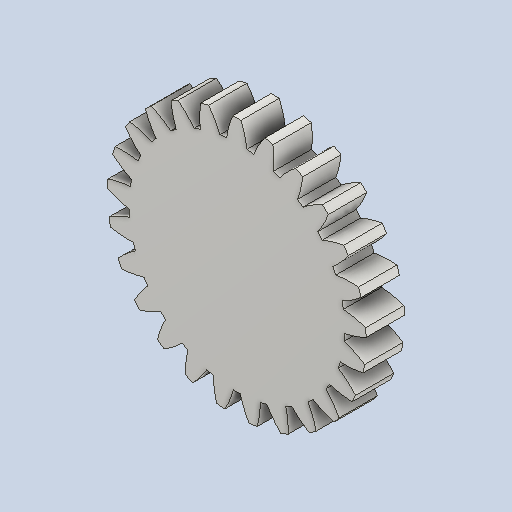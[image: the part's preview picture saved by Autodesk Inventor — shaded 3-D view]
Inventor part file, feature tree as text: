
AUTODESK INVENTOR PART (.ipt)
format: ipt  version: 2024 (Build 280153000, 153)  size: 251,904 bytes
history: native  units: mm (DEFAULTED — no unit token found)
features: plane x3, other x3, extrude x1, sketch x1
ambient origin geometry x8: Origin, YZ Plane, XZ Plane, XY Plane, X Axis, Y Axis, Z Axis, Center Point
bodies: Solid1 (feature_tree)
feature tree (8):
  extrude  "Extrusion1"  Depth=20.0mm TaperAngle=0.0deg
  plane  "Work Plane2"
  plane  "Work Plane8"
  plane  "Work Plane9"
  other  "Spur Gear"
  sketch  "Sketch1"  dims[d0=135.0mm d1=20.0mm d2=0.0mm d3=125.0mm d4=10.0mm d5=0.0mm d16=140.0mm d17=0.0mm d34=1.256637mm d39=0.0mm d41=0.0mm d43=140.0mm d46=140.0mm d47=0.0mm d48=0.0mm]
  other  "Srf1"
  other  "Pitch Diameter"
